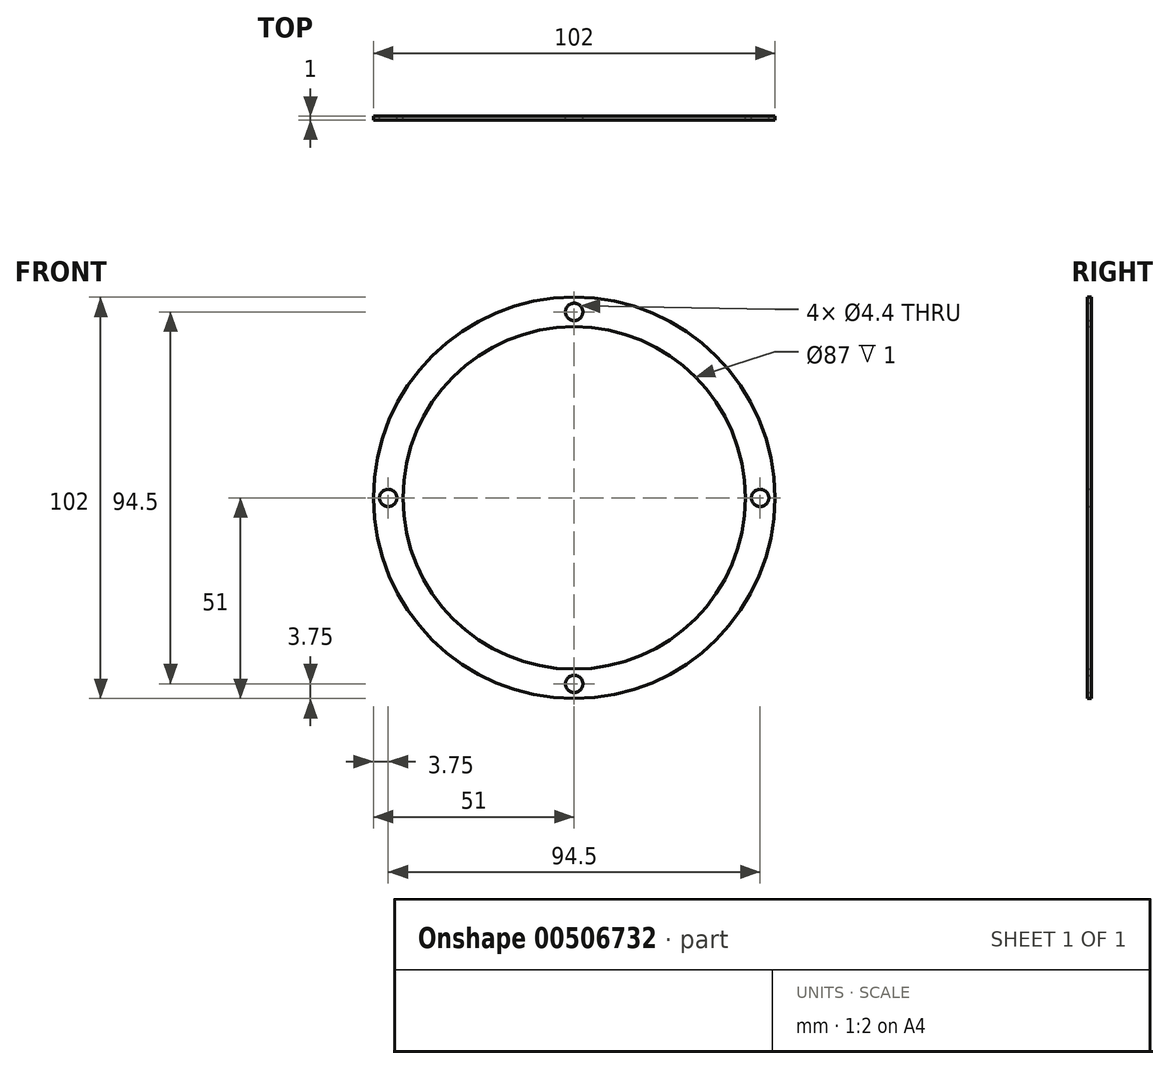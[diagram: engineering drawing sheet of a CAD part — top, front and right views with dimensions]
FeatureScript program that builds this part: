
annotation { "Feature Type Name" : "Feature", "Feature Type Description" : "" }
export const myFeature = defineFeature(function(context is Context, id is Id, definition is map)
    precondition{}
    {
        {
            var Q0;
            Q0=qCreatedBy(makeId("Front.planeOp"),FACE);
            var sketch = newSketch(context, id + "F0", { "sketchPlane" : qUnion([Q0])});
            skCircle(sketch, "E0", {"center": v(0, 0) * mm, "radius": 51 * mm});
            skCircle(sketch, "E1", {"center": v(0, 0) * mm, "radius": 43.5 * mm});
            skLineSegment(sketch, "E2", {"start": v(0, 51) * mm, "end": v(0, 43.5) * mm, "construction": true});
            skCircle(sketch, "E3", {"center": v(0, 47.25) * mm, "radius": 2.2 * mm, "construction": true});
            skCircle(sketch, "E4.1.0", {"center": v(-47.25, 0) * mm, "radius": 2.2 * mm, "construction": true});
            skCircle(sketch, "E4.2.0", {"center": v(0, -47.25) * mm, "radius": 2.2 * mm, "construction": true});
            skCircle(sketch, "E4.3.0", {"center": v(47.25, 0) * mm, "radius": 2.2 * mm, "construction": true});
            skSolve(sketch);
        }
        {
            var Q0;
            Q0=makeQuery(id+"F0.imprint","IMPRINT",FACE,{"disambiguationData":[TD([[makeQuery(id+"F0.imprint","IMPRINT",EDGE,{"derivedFrom":sQuery(id+"F0.wireOp",EDGE,"E0")}),1.0]])]});
            extrude(context, id + "F1", {"entities" : qUnion([Q0]), "depth" : 1 * mm, "offsetDistance" : 25 * mm});
        }
        {
            var Q0;
            Q0=sQuery(id+"F0.wireOp",VERTEX,"E3.center");
            var Q1;
            Q1=sQuery(id+"F0.wireOp",VERTEX,"E4.1.0.center");
            var Q2;
            Q2=sQuery(id+"F0.wireOp",VERTEX,"E4.2.0.center");
            var Q3;
            Q3=sQuery(id+"F0.wireOp",VERTEX,"E4.3.0.center");
            var Q4;
            Q4=makeQuery(id+"F1.opExtrude","SWEPT_BODY",BODY,{"disambiguationData":[OSD([sQuery(id+"F0.wireOp",EDGE,"E0"),sQuery(id+"F0.wireOp",EDGE,"E1")])]});
            hole(context, id + "F2", {"style" : HoleStyle.SIMPLE, "endStyle" : HoleEndStyle.BLIND, "oppositeDirection" : true, "standardTappedOrClearance" : lookupTablePath({ "standard" : "ISO", "fit" : "Normal", "size" : "M4", "type" : "Clearance" }), "standardBlindInLast" : lookupTablePath({ "fit" : "Standard", "standard" : "ISO", "size" : "M4", "type" : "Clearance" }), "holeDiameter" : 4.4 * mm, "majorDiameter" : 5 * mm, "holeDepth" : 2.5 * mm, "isTappedThrough" : true, "tappedDepth" : 12 * mm, "tapClearance" : 3, "locations" : qUnion([Q0, Q1, Q2, Q3]), "scope" : qUnion([Q4])});
        }
    });
